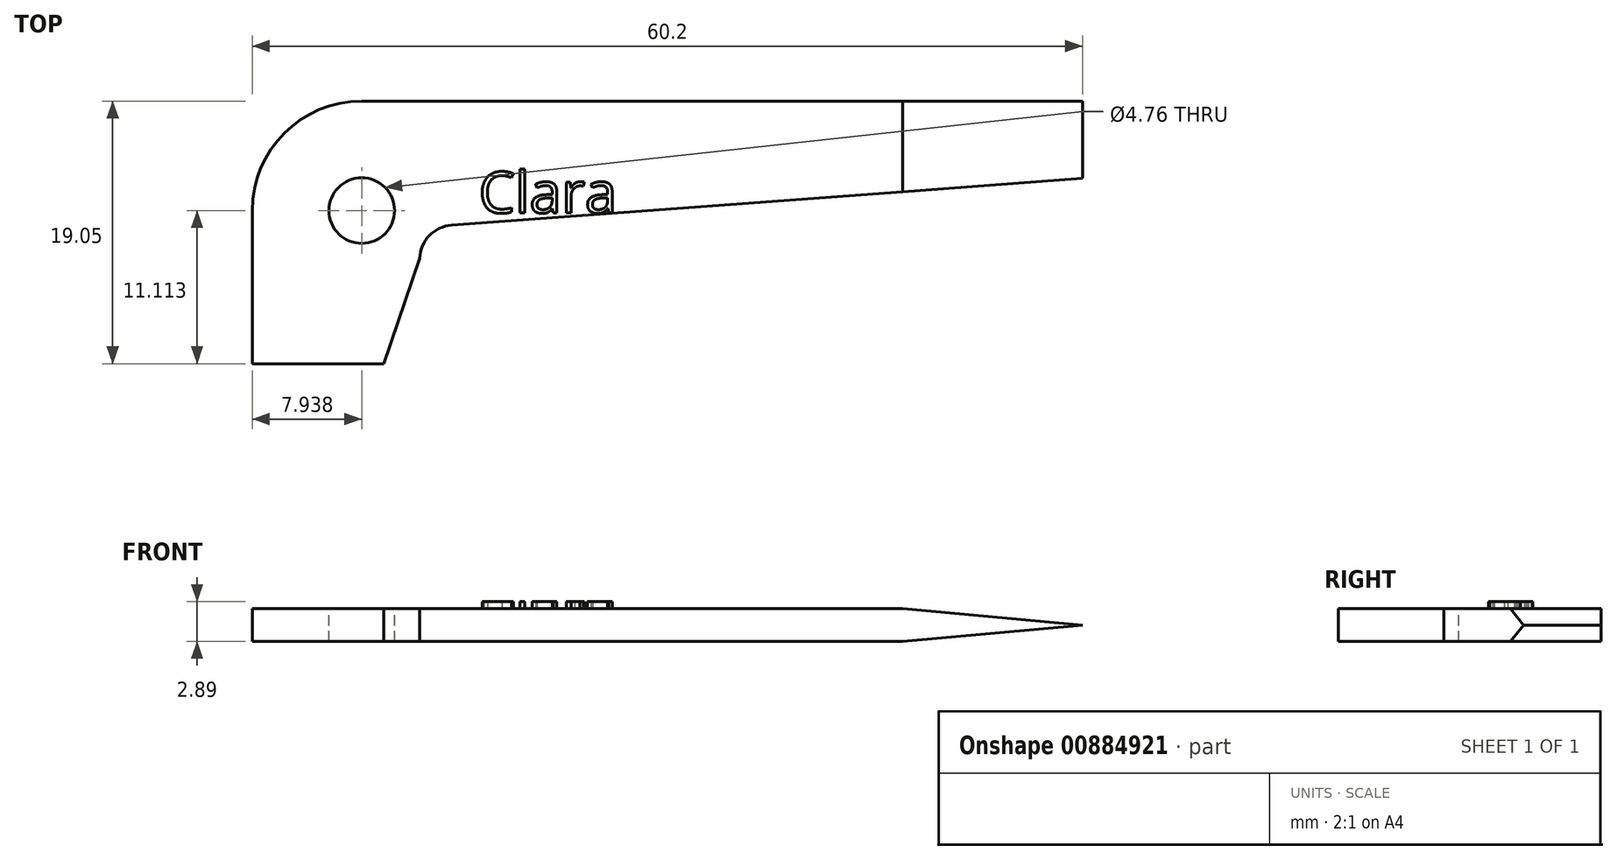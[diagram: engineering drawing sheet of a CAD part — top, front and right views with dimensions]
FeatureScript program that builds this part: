
annotation { "Feature Type Name" : "Feature", "Feature Type Description" : "" }
export const myFeature = defineFeature(function(context is Context, id is Id, definition is map)
    precondition{}
    {
        {
            var Q0;
            Q0=qCreatedBy(makeId("Top.planeOp"),FACE);
            var sketch = newSketch(context, id + "F0", { "sketchPlane" : qUnion([Q0])});
            skLineSegment(sketch, "E0.top", {"start": v(7.94, 19.05) * mm, "end": v(60.2, 19.05) * mm});
            skLineSegment(sketch, "E0.left", {"start": v(0, 0) * mm, "end": v(0, 11.11) * mm});
            skLineSegment(sketch, "E1", {"start": v(9.53, 0) * mm, "end": v(12.14, 7.64) * mm});
            skLineSegment(sketch, "E2", {"start": v(60.2, 13.44) * mm, "end": v(14.47, 10.06) * mm});
            skArc(sketch, "E3", {"start": v(14.47, 10.06) * mm, "mid": v(12.84, 9.3) * mm, "end": v(12.14, 7.64) * mm});
            skPoint(sketch, "E4.visualSharp", {"position": v(0, 19.05) * mm});
            skArc(sketch, "E4.filletArc", {"start": v(7.94, 19.05) * mm, "mid": v(2.32, 16.73) * mm, "end": v(0, 11.11) * mm});
            skLineSegment(sketch, "E5", {"start": v(60.2, 19.05) * mm, "end": v(60.2, 13.44) * mm});
            skLineSegment(sketch, "E6", {"start": v(0, 0) * mm, "end": v(9.53, 0) * mm});
            skSolve(sketch);
        }
        {
            var Q0;
            Q0=makeQuery(id+"F0.imprint","IMPRINT",FACE,{"disambiguationData":[TD([[makeQuery(id+"F0.imprint","IMPRINT",EDGE,{"derivedFrom":sQuery(id+"F0.wireOp",EDGE,"E0.top")}),-1.0]])]});
            extrude(context, id + "F1", {"entities" : qUnion([Q0]), "depth" : 2.38 * mm, "offsetDistance" : 25.4 * mm});
        }
        {
            var Q0;
            Q0=makeQuery(id+"F1.opExtrude","CAP_FACE",FACE,{"disambiguationData":[OSD([sQuery(id+"F0.wireOp",EDGE,"E0.top"),sQuery(id+"F0.wireOp",EDGE,"E0.left"),sQuery(id+"F0.wireOp",EDGE,"E1"),sQuery(id+"F0.wireOp",EDGE,"E2"),sQuery(id+"F0.wireOp",EDGE,"E3"),sQuery(id+"F0.wireOp",EDGE,"E4.filletArc"),sQuery(id+"F0.wireOp",EDGE,"E5"),sQuery(id+"F0.wireOp",EDGE,"E6")])],"isStart":false});
            var sketch = newSketch(context, id + "F2", { "sketchPlane" : qUnion([Q0])});
            skCircle(sketch, "E7", {"center": v(7.94, 11.11) * mm, "radius": 2.38 * mm});
            skSolve(sketch);
        }
        {
            var Q0;
            Q0=makeQuery(id+"F2.imprint","IMPRINT",FACE,{"disambiguationData":[TD([[makeQuery(id+"F2.imprint","IMPRINT",EDGE,{"derivedFrom":sQuery(id+"F2.wireOp",EDGE,"E7")}),1.0]])]});
            extrude(context, id + "F3", {"entities" : qUnion([Q0]), "operationType" : NewBodyOperationType.REMOVE, "oppositeDirection" : true, "depth" : 2.38 * mm, "offsetDistance" : 25.4 * mm});
        }
        {
            var Q0;
            Q0=makeQuery(id+"F1.opExtrude","SWEPT_FACE",FACE,{"disambiguationData":[OSD([sQuery(id+"F0.wireOp",EDGE,"E0.top")])]});
            var sketch = newSketch(context, id + "F4", { "sketchPlane" : qUnion([Q0])});
            skLineSegment(sketch, "E8", {"start": v(-47.15, 0) * mm, "end": v(-60.2, 1.2) * mm});
            skLineSegment(sketch, "E9", {"start": v(-60.2, 1.2) * mm, "end": v(-43.18, 1.2) * mm});
            skLineSegment(sketch, "E10.MirrorCS", {"start": v(-47.15, 2.38) * mm, "end": v(-60.2, 1.2) * mm});
            skSolve(sketch);
        }
        {
            var Q0;
            Q0 = qSketchRegion(id + "F4", true);
            var Q1;
            {var subQ0=sQuery(id+"F4.wireOp",EDGE,"E8");Q1=makeQuery(id+"F4.imprint","IMPRINT",FACE,{"disambiguationData":[TD([[makeQuery(id+"F4.imprint","IMPRINT",EDGE,{"derivedFrom":subQ0}),1.0]])]});}
            var Q2;
            {var subQ0=sQuery(id+"F4.wireOp",EDGE,"E10.MirrorCS");Q2=makeQuery(id+"F4.imprint","IMPRINT",FACE,{"disambiguationData":[TD([[makeQuery(id+"F4.imprint","IMPRINT",EDGE,{"derivedFrom":subQ0}),-1.0]])]});}
            extrude(context, id + "F5", {"entities" : qUnion([Q0, Q1, Q2]), "operationType" : NewBodyOperationType.REMOVE, "oppositeDirection" : true, "depth" : 25.4 * mm, "offsetDistance" : 25.4 * mm});
        }
        {
            var Q0;
            Q0=makeQuery(id+"F1.opExtrude","CAP_FACE",FACE,{"disambiguationData":[OSD([sQuery(id+"F0.wireOp",EDGE,"E0.top"),sQuery(id+"F0.wireOp",EDGE,"E0.left"),sQuery(id+"F0.wireOp",EDGE,"E1"),sQuery(id+"F0.wireOp",EDGE,"E2"),sQuery(id+"F0.wireOp",EDGE,"E3"),sQuery(id+"F0.wireOp",EDGE,"E4.filletArc"),sQuery(id+"F0.wireOp",EDGE,"E5"),sQuery(id+"F0.wireOp",EDGE,"E6")])],"isStart":false});
            var sketch = newSketch(context, id + "F6", { "sketchPlane" : qUnion([Q0])});
            skText(sketch, "E11", { "text": "Clara", "fontName": "OpenSans-Regular.ttf"});
            const initialGuessF6  = {"E11": [0.01642, 0.01094, 1, 0, 0.003]};
            skSetInitialGuess(sketch, initialGuessF6);
            skSolve(sketch);
        }
        {
            var Q0;
            Q0 = qSketchRegion(id + "F6", true);
            extrude(context, id + "F7", {"entities" : qUnion([Q0]), "operationType" : NewBodyOperationType.ADD, "depth" : 0.5 * mm, "offsetDistance" : 25.4 * mm});
        }
    });
